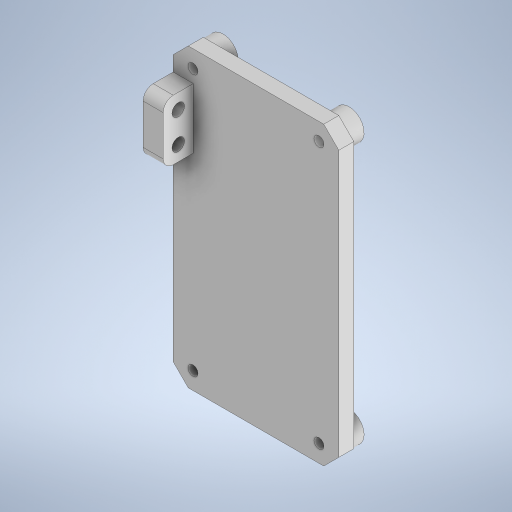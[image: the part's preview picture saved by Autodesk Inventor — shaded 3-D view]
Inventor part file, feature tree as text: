
AUTODESK INVENTOR PART (.ipt)
format: ipt  version: 2023 (Build 270158000, 158)  size: 286,720 bytes
history: native  units: mm
features: sketch x3, extrude x3, projected_geometry x3, other x1, hole x1, fillet x1, chamfer x1
ambient origin geometry x8: Origin, YZ Plane, XZ Plane, XY Plane, X Axis, Y Axis, Z Axis, Center Point
bodies: Body1 (feature_tree)
feature tree (13):
  other  "솔리드1"
  sketch  "스케치1"
  extrude  "돌출1"  Depth=33.0mm
  extrude  "돌출2"  Depth=59.0mm
  hole  "구멍1"  [1 undecoded]
  extrude  "돌출3"  Depth=57.6mm
  fillet  "모깎기1"  Radius=6.0mm
  chamfer  "모따기1"  Distance=25.1mm
  sketch  "스케치3"
  projected_geometry  "투영된 루프1"
  projected_geometry  "투영된 루프2"
  projected_geometry  "투영된 루프3"
  sketch  "스케치4"
note: 1 required parameter value undecoded (feature->parameter linkage not recoverable at this tier; creation-order binding heuristic only, values carry confidence <= 0.55)
